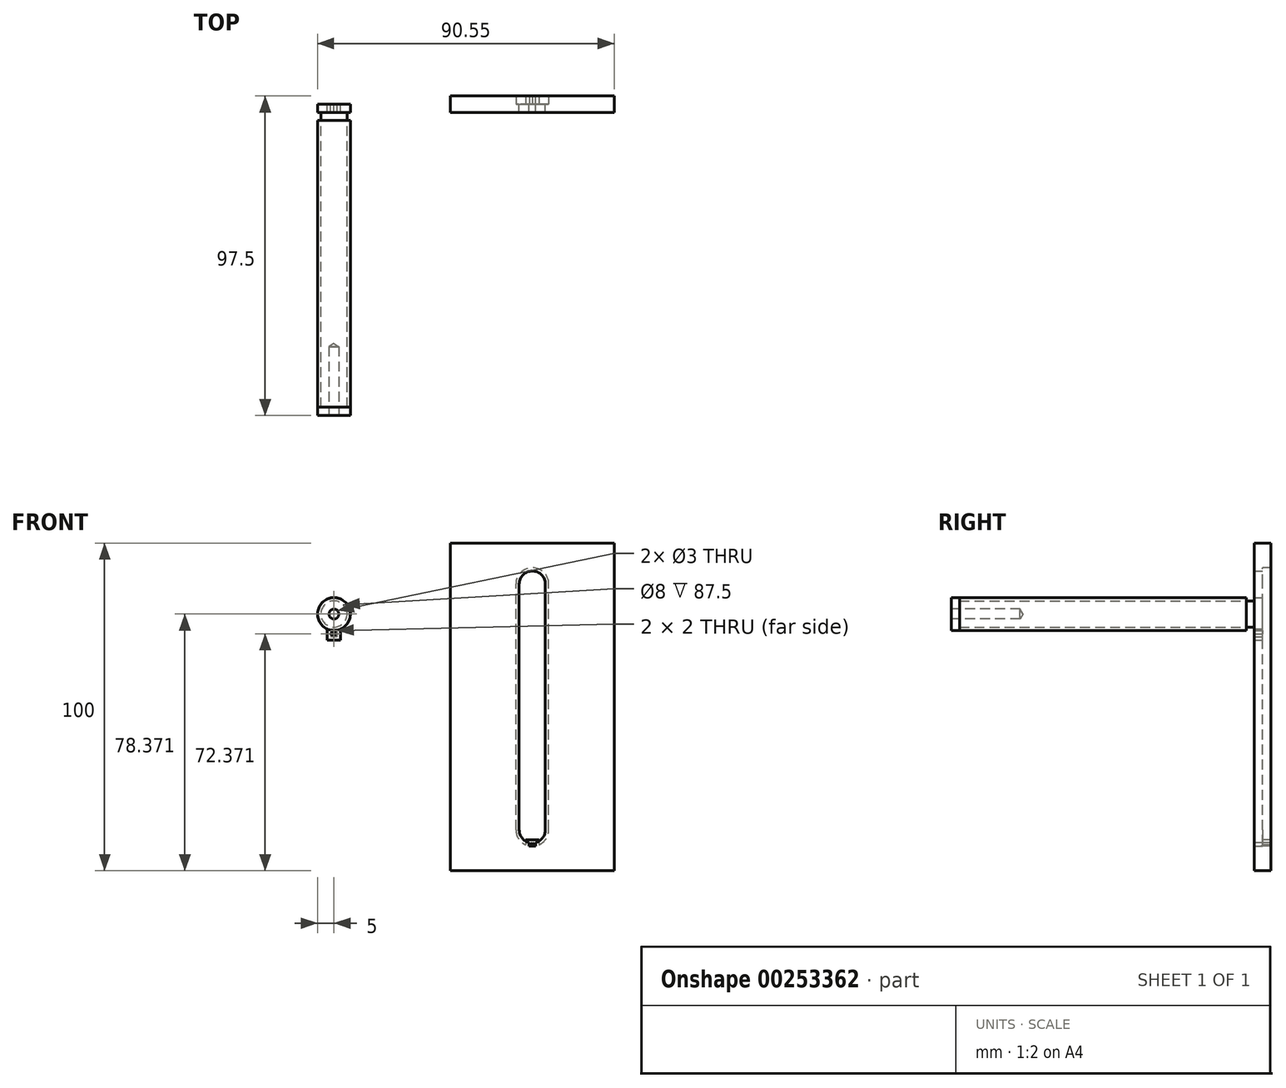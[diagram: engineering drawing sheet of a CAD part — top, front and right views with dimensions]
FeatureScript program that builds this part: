
annotation { "Feature Type Name" : "Feature", "Feature Type Description" : "" }
export const myFeature = defineFeature(function(context is Context, id is Id, definition is map)
    precondition{}
    {
        {
            var Q0;
            Q0=qCreatedBy(makeId("Front.planeOp"),FACE);
            var sketch = newSketch(context, id + "F0", { "sketchPlane" : qUnion([Q0])});
            skLineSegment(sketch, "E0.bottom", {"start": v(25, -50) * mm, "end": v(-25, -50) * mm});
            skLineSegment(sketch, "E0.top", {"start": v(25, 50) * mm, "end": v(-25, 50) * mm});
            skLineSegment(sketch, "E0.left", {"start": v(25, -50) * mm, "end": v(25, 50) * mm});
            skLineSegment(sketch, "E0.right", {"start": v(-25, -50) * mm, "end": v(-25, 50) * mm});
            skPoint(sketch, "E0.middle", {"position": v(0, 0) * mm});
            skArc(sketch, "E1", {"start": v(5, 37.5) * mm, "mid": v(0, 42.5) * mm, "end": v(-5, 37.5) * mm});
            skArc(sketch, "E2", {"start": v(-5, -37.5) * mm, "mid": v(0, -42.5) * mm, "end": v(5, -37.5) * mm});
            skLineSegment(sketch, "E3.left", {"start": v(5, -37.5) * mm, "end": v(5, 37.5) * mm});
            skLineSegment(sketch, "E3.right", {"start": v(-5, -37.5) * mm, "end": v(-5, 37.5) * mm});
            skPoint(sketch, "E4.end.orphan", {"position": v(0, 50) * mm});
            skArc(sketch, "E5", {"start": v(4, 37.5) * mm, "mid": v(0, 41.5) * mm, "end": v(-4, 37.5) * mm});
            skArc(sketch, "E6", {"start": v(-4, -37.5) * mm, "mid": v(0, -41.5) * mm, "end": v(4, -37.5) * mm});
            skLineSegment(sketch, "E7.left", {"start": v(-4, -37.5) * mm, "end": v(-4, 37.5) * mm});
            skLineSegment(sketch, "E7.right", {"start": v(4, -37.5) * mm, "end": v(4, 37.5) * mm});
            skLineSegment(sketch, "E8", {"start": v(0, -41.5) * mm, "end": v(0, -42.5) * mm});
            skLineSegment(sketch, "E9", {"start": v(0, -42.5) * mm, "end": v(-1, -42.5) * mm});
            skLineSegment(sketch, "E10", {"start": v(-1, -42.5) * mm, "end": v(0, -41.5) * mm});
            skLineSegment(sketch, "E11", {"start": v(0, -42.5) * mm, "end": v(1, -42.5) * mm});
            skLineSegment(sketch, "E12", {"start": v(1, -42.5) * mm, "end": v(0, -41.5) * mm});
            skLineSegment(sketch, "E13", {"start": v(0, -41.5) * mm, "end": v(0, -40.5) * mm});
            skLineSegment(sketch, "E14", {"start": v(0, -40.5) * mm, "end": v(1, -40.5) * mm});
            skLineSegment(sketch, "E15", {"start": v(1, -40.5) * mm, "end": v(1, -42.5) * mm});
            skLineSegment(sketch, "E16", {"start": v(0, -40.5) * mm, "end": v(-1, -40.5) * mm});
            skLineSegment(sketch, "E17", {"start": v(-1, -40.5) * mm, "end": v(-1, -42.5) * mm});
            skLineSegment(sketch, "E18", {"start": v(-1, -40.5) * mm, "end": v(-2, -40.5) * mm});
            skLineSegment(sketch, "E19", {"start": v(-2, -40.5) * mm, "end": v(-2, -42.5) * mm});
            skLineSegment(sketch, "E20", {"start": v(-2, -42.5) * mm, "end": v(-1, -42.5) * mm});
            skLineSegment(sketch, "E21", {"start": v(1, -40.5) * mm, "end": v(2, -40.5) * mm});
            skLineSegment(sketch, "E22", {"start": v(2, -40.5) * mm, "end": v(2, -42.5) * mm});
            skLineSegment(sketch, "E23", {"start": v(2, -42.5) * mm, "end": v(1, -42.5) * mm});
            skSolve(sketch);
        }
        {
            var Q0;
            Q0 = qSketchRegion(id + "F0", true);
            var Q1;
            {var subQ0=sQuery(id+"F0.wireOp",EDGE,"E9");Q1=makeQuery(id+"F0.imprint","IMPRINT",FACE,{"disambiguationData":[TD([[makeQuery(id+"F0.imprint","IMPRINT",EDGE,{"derivedFrom":subQ0}),-1.0]])]});}
            var Q2;
            {var subQ0=sQuery(id+"F0.wireOp",EDGE,"E17");var subQ1=sQuery(id+"F0.wireOp",EDGE,"E2");var subQ2=makeQuery(id+"F0.imprint","INTERSECT",VERTEX,{"derivedFrom":[subQ1,subQ0]});Q2=makeQuery(id+"F0.imprint","IMPRINT",FACE,{"disambiguationData":[TD([[makeQuery(id+"F0.imprint","IMPRINT",EDGE,{"disambiguationData":[TD([[subQ2,-1.0]])],"derivedFrom":subQ1}),-1.0]])]});}
            var Q3;
            {var subQ0=sQuery(id+"F0.wireOp",EDGE,"E12");var subQ1=sQuery(id+"F0.wireOp",EDGE,"E2");var subQ2=makeQuery(id+"F0.imprint","INTERSECT",VERTEX,{"derivedFrom":[subQ1,subQ0]});Q3=makeQuery(id+"F0.imprint","IMPRINT",FACE,{"disambiguationData":[TD([[makeQuery(id+"F0.imprint","IMPRINT",EDGE,{"disambiguationData":[TD([[subQ2,-1.0]])],"derivedFrom":subQ1}),-1.0]])]});}
            var Q4;
            {var subQ0=sQuery(id+"F0.wireOp",EDGE,"E11");Q4=makeQuery(id+"F0.imprint","IMPRINT",FACE,{"disambiguationData":[TD([[makeQuery(id+"F0.imprint","IMPRINT",EDGE,{"derivedFrom":subQ0}),1.0]])]});}
            var Q5;
            {var subQ0=sQuery(id+"F0.wireOp",EDGE,"E12");var subQ1=sQuery(id+"F0.wireOp",EDGE,"E2");var subQ2=makeQuery(id+"F0.imprint","INTERSECT",VERTEX,{"derivedFrom":[subQ1,subQ0]});Q5=makeQuery(id+"F0.imprint","IMPRINT",FACE,{"disambiguationData":[TD([[makeQuery(id+"F0.imprint","IMPRINT",EDGE,{"disambiguationData":[TD([[subQ2,-1.0]])],"derivedFrom":subQ1}),1.0]])]});}
            var Q6;
            {var subQ0=sQuery(id+"F0.wireOp",EDGE,"E13");Q6=makeQuery(id+"F0.imprint","IMPRINT",FACE,{"disambiguationData":[TD([[makeQuery(id+"F0.imprint","IMPRINT",EDGE,{"derivedFrom":subQ0}),-1.0]])]});}
            var Q7;
            {var subQ0=sQuery(id+"F0.wireOp",EDGE,"E13");Q7=makeQuery(id+"F0.imprint","IMPRINT",FACE,{"disambiguationData":[TD([[makeQuery(id+"F0.imprint","IMPRINT",EDGE,{"derivedFrom":subQ0}),1.0]])]});}
            var Q8;
            {var subQ0=sQuery(id+"F0.wireOp",EDGE,"E17");var subQ1=sQuery(id+"F0.wireOp",EDGE,"E2");var subQ2=makeQuery(id+"F0.imprint","INTERSECT",VERTEX,{"derivedFrom":[subQ1,subQ0]});Q8=makeQuery(id+"F0.imprint","IMPRINT",FACE,{"disambiguationData":[TD([[makeQuery(id+"F0.imprint","IMPRINT",EDGE,{"disambiguationData":[TD([[subQ2,-1.0]])],"derivedFrom":subQ1}),1.0]])]});}
            var Q9;
            {var subQ5=sQuery(id+"F0.wireOp",EDGE,"E18");Q9=makeQuery(id+"F0.imprint","IMPRINT",FACE,{"disambiguationData":[TD([[makeQuery(id+"F0.imprint","IMPRINT",EDGE,{"derivedFrom":subQ5}),1.0]])]});}
            var Q10;
            {var subQ0=sQuery(id+"F0.wireOp",EDGE,"E19");var subQ1=sQuery(id+"F0.wireOp",EDGE,"E2");var subQ2=makeQuery(id+"F0.imprint","INTERSECT",VERTEX,{"derivedFrom":[subQ1,subQ0]});Q10=makeQuery(id+"F0.imprint","IMPRINT",FACE,{"disambiguationData":[TD([[makeQuery(id+"F0.imprint","IMPRINT",EDGE,{"disambiguationData":[TD([[subQ2,-1.0]])],"derivedFrom":subQ1}),1.0]])]});}
            var Q11;
            {var subQ5=sQuery(id+"F0.wireOp",EDGE,"E20");Q11=makeQuery(id+"F0.imprint","IMPRINT",FACE,{"disambiguationData":[TD([[makeQuery(id+"F0.imprint","IMPRINT",EDGE,{"derivedFrom":subQ5}),1.0]])]});}
            var Q12;
            {var subQ5=sQuery(id+"F0.wireOp",EDGE,"E21");Q12=makeQuery(id+"F0.imprint","IMPRINT",FACE,{"disambiguationData":[TD([[makeQuery(id+"F0.imprint","IMPRINT",EDGE,{"derivedFrom":subQ5}),-1.0]])]});}
            var Q13;
            {var subQ0=sQuery(id+"F0.wireOp",EDGE,"E15");var subQ1=sQuery(id+"F0.wireOp",EDGE,"E2");var subQ2=makeQuery(id+"F0.imprint","INTERSECT",VERTEX,{"derivedFrom":[subQ1,subQ0]});Q13=makeQuery(id+"F0.imprint","IMPRINT",FACE,{"disambiguationData":[TD([[makeQuery(id+"F0.imprint","IMPRINT",EDGE,{"disambiguationData":[TD([[subQ2,-1.0]])],"derivedFrom":subQ1}),1.0]])]});}
            var Q14;
            {var subQ5=sQuery(id+"F0.wireOp",EDGE,"E23");Q14=makeQuery(id+"F0.imprint","IMPRINT",FACE,{"disambiguationData":[TD([[makeQuery(id+"F0.imprint","IMPRINT",EDGE,{"derivedFrom":subQ5}),-1.0]])]});}
            extrude(context, id + "F1", {"entities" : qUnion([Q0, Q1, Q2, Q3, Q4, Q5, Q6, Q7, Q8, Q9, Q10, Q11, Q12, Q13, Q14]), "oppositeDirection" : true, "depth" : 2.5 * mm});
        }
        {
            var Q0;
            Q0=makeQuery(id+"F0.imprint","IMPRINT",FACE,{"disambiguationData":[TD([[makeQuery(id+"F0.imprint","IMPRINT",EDGE,{"derivedFrom":sQuery(id+"F0.wireOp",EDGE,"E0.bottom")}),-1.0]])]});
            var Q1;
            Q1=makeQuery(id+"F0.imprint","IMPRINT",FACE,{"disambiguationData":[TD([[makeQuery(id+"F0.imprint","IMPRINT",EDGE,{"derivedFrom":sQuery(id+"F0.wireOp",EDGE,"E1")}),1.0]])]});
            var Q2;
            {var subQ0=sQuery(id+"F0.wireOp",EDGE,"E19");var subQ1=sQuery(id+"F0.wireOp",EDGE,"E2");var subQ2=makeQuery(id+"F0.imprint","INTERSECT",VERTEX,{"derivedFrom":[subQ1,subQ0]});Q2=makeQuery(id+"F0.imprint","IMPRINT",FACE,{"disambiguationData":[TD([[makeQuery(id+"F0.imprint","IMPRINT",EDGE,{"disambiguationData":[TD([[subQ2,-1.0]])],"derivedFrom":subQ1}),1.0]])]});}
            var Q3;
            {var subQ0=sQuery(id+"F0.wireOp",EDGE,"E15");var subQ1=sQuery(id+"F0.wireOp",EDGE,"E2");var subQ2=makeQuery(id+"F0.imprint","INTERSECT",VERTEX,{"derivedFrom":[subQ1,subQ0]});Q3=makeQuery(id+"F0.imprint","IMPRINT",FACE,{"disambiguationData":[TD([[makeQuery(id+"F0.imprint","IMPRINT",EDGE,{"disambiguationData":[TD([[subQ2,-1.0]])],"derivedFrom":subQ1}),1.0]])]});}
            var Q4;
            {var subQ5=sQuery(id+"F0.wireOp",EDGE,"E23");Q4=makeQuery(id+"F0.imprint","IMPRINT",FACE,{"disambiguationData":[TD([[makeQuery(id+"F0.imprint","IMPRINT",EDGE,{"derivedFrom":subQ5}),-1.0]])]});}
            var Q5;
            {var subQ5=sQuery(id+"F0.wireOp",EDGE,"E20");Q5=makeQuery(id+"F0.imprint","IMPRINT",FACE,{"disambiguationData":[TD([[makeQuery(id+"F0.imprint","IMPRINT",EDGE,{"derivedFrom":subQ5}),1.0]])]});}
            var Q6;
            {var subQ0=sQuery(id+"F0.wireOp",EDGE,"E17");var subQ1=sQuery(id+"F0.wireOp",EDGE,"E2");var subQ2=makeQuery(id+"F0.imprint","INTERSECT",VERTEX,{"derivedFrom":[subQ1,subQ0]});Q6=makeQuery(id+"F0.imprint","IMPRINT",FACE,{"disambiguationData":[TD([[makeQuery(id+"F0.imprint","IMPRINT",EDGE,{"disambiguationData":[TD([[subQ2,-1.0]])],"derivedFrom":subQ1}),-1.0]])]});}
            var Q7;
            {var subQ0=sQuery(id+"F0.wireOp",EDGE,"E9");Q7=makeQuery(id+"F0.imprint","IMPRINT",FACE,{"disambiguationData":[TD([[makeQuery(id+"F0.imprint","IMPRINT",EDGE,{"derivedFrom":subQ0}),-1.0]])]});}
            var Q8;
            {var subQ0=sQuery(id+"F0.wireOp",EDGE,"E12");var subQ1=sQuery(id+"F0.wireOp",EDGE,"E2");var subQ2=makeQuery(id+"F0.imprint","INTERSECT",VERTEX,{"derivedFrom":[subQ1,subQ0]});Q8=makeQuery(id+"F0.imprint","IMPRINT",FACE,{"disambiguationData":[TD([[makeQuery(id+"F0.imprint","IMPRINT",EDGE,{"disambiguationData":[TD([[subQ2,-1.0]])],"derivedFrom":subQ1}),-1.0]])]});}
            var Q9;
            {var subQ0=sQuery(id+"F0.wireOp",EDGE,"E11");Q9=makeQuery(id+"F0.imprint","IMPRINT",FACE,{"disambiguationData":[TD([[makeQuery(id+"F0.imprint","IMPRINT",EDGE,{"derivedFrom":subQ0}),1.0]])]});}
            extrude(context, id + "F2", {"entities" : qUnion([Q0, Q1, Q2, Q3, Q4, Q5, Q6, Q7, Q8, Q9]), "operationType" : NewBodyOperationType.ADD, "depth" : 2.5 * mm});
        }
        {
            var Q0;
            Q0=qCreatedBy(makeId("Front.planeOp"),FACE);
            var sketch = newSketch(context, id + "F3", { "sketchPlane" : qUnion([Q0])});
            skCircle(sketch, "E24", {"center": v(-60.55, 28.37) * mm, "radius": 5 * mm});
            skCircle(sketch, "E25", {"center": v(-60.55, 28.37) * mm, "radius": 4 * mm});
            skLineSegment(sketch, "E26", {"start": v(-59.55, 22.37) * mm, "end": v(-59.55, 21.37) * mm});
            skLineSegment(sketch, "E27", {"start": v(-59.55, 21.37) * mm, "end": v(-61.55, 21.37) * mm});
            skLineSegment(sketch, "E28", {"start": v(-61.55, 21.37) * mm, "end": v(-61.55, 22.37) * mm});
            skLineSegment(sketch, "E29", {"start": v(-59.55, 22.37) * mm, "end": v(-59.55, 23.47) * mm});
            skPoint(sketch, "E30.end.orphan", {"position": v(-60.55, 22.37) * mm});
            skPoint(sketch, "E30.start.orphan", {"position": v(-60.55, 23.37) * mm});
            skLineSegment(sketch, "E31", {"start": v(-60.55, 23.37) * mm, "end": v(-59.55, 22.37) * mm});
            skLineSegment(sketch, "E32", {"start": v(-61.55, 22.37) * mm, "end": v(-61.55, 23.47) * mm});
            skLineSegment(sketch, "E33", {"start": v(-60.55, 23.37) * mm, "end": v(-61.55, 22.37) * mm});
            skLineSegment(sketch, "E34", {"start": v(-61.55, 21.37) * mm, "end": v(-62.55, 21.37) * mm});
            skLineSegment(sketch, "E35", {"start": v(-62.55, 21.37) * mm, "end": v(-62.55, 23.79) * mm});
            skLineSegment(sketch, "E36", {"start": v(-59.55, 21.37) * mm, "end": v(-58.55, 21.37) * mm});
            skLineSegment(sketch, "E37", {"start": v(-58.55, 21.37) * mm, "end": v(-58.55, 23.79) * mm});
            skLineSegment(sketch, "E38", {"start": v(-62.55, 21.37) * mm, "end": v(-62.55, 20.37) * mm});
            skLineSegment(sketch, "E39", {"start": v(-62.55, 20.37) * mm, "end": v(-58.55, 20.37) * mm});
            skLineSegment(sketch, "E40", {"start": v(-58.55, 20.37) * mm, "end": v(-58.55, 21.37) * mm});
            skLineSegment(sketch, "E41", {"start": v(-61.55, 22.37) * mm, "end": v(-60.55, 21.37) * mm});
            skLineSegment(sketch, "E42", {"start": v(-60.55, 21.37) * mm, "end": v(-59.55, 22.37) * mm});
            skSolve(sketch);
        }
        {
            var Q0;
            Q0 = qSketchRegion(id + "F3", true);
            var Q1;
            {var subQ0=sQuery(id+"F3.wireOp",EDGE,"E28");Q1=makeQuery(id+"F3.imprint","IMPRINT",FACE,{"disambiguationData":[TD([[makeQuery(id+"F3.imprint","IMPRINT",EDGE,{"derivedFrom":subQ0}),-1.0]])]});}
            var Q2;
            {var subQ2=sQuery(id+"F3.wireOp",EDGE,"E32");Q2=makeQuery(id+"F3.imprint","IMPRINT",FACE,{"disambiguationData":[TD([[makeQuery(id+"F3.imprint","IMPRINT",EDGE,{"derivedFrom":subQ2}),-1.0]])]});}
            var Q3;
            {var subQ0=sQuery(id+"F3.wireOp",EDGE,"E29");Q3=makeQuery(id+"F3.imprint","IMPRINT",FACE,{"disambiguationData":[TD([[makeQuery(id+"F3.imprint","IMPRINT",EDGE,{"derivedFrom":subQ0}),1.0]])]});}
            var Q4;
            {var subQ0=sQuery(id+"F3.wireOp",EDGE,"E26");Q4=makeQuery(id+"F3.imprint","IMPRINT",FACE,{"disambiguationData":[TD([[makeQuery(id+"F3.imprint","IMPRINT",EDGE,{"derivedFrom":subQ0}),-1.0]])]});}
            extrude(context, id + "F4", {"entities" : qUnion([Q0, Q1, Q2, Q3, Q4]), "depth" : 2.5 * mm});
        }
        {
            var Q0;
            Q0=makeQuery(id+"F3.imprint","IMPRINT",FACE,{"disambiguationData":[TD([[makeQuery(id+"F3.imprint","IMPRINT",EDGE,{"derivedFrom":sQuery(id+"F3.wireOp",EDGE,"E25")}),1.0]])]});
            extrude(context, id + "F5", {"entities" : qUnion([Q0]), "operationType" : NewBodyOperationType.ADD, "depth" : 92.5 * mm});
        }
        {
            var Q0;
            Q0=makeQuery(id+"F5.opExtrude","CAP_FACE",FACE,{"disambiguationData":[OSD([sQuery(id+"F3.wireOp",EDGE,"E25")])],"isStart":false});
            var sketch = newSketch(context, id + "F6", { "sketchPlane" : qUnion([Q0])});
            skCircle(sketch, "E43", {"center": v(-60.55, 28.37) * mm, "radius": 4 * mm});
            skSolve(sketch);
        }
        {
            var Q0;
            Q0=makeQuery(id+"F3.imprint","IMPRINT",FACE,{"disambiguationData":[TD([[makeQuery(id+"F3.imprint","IMPRINT",EDGE,{"derivedFrom":sQuery(id+"F3.wireOp",EDGE,"E25")}),-1.0]])]});
            extrude(context, id + "F7", {"entities" : qUnion([Q0]), "depth" : 92.5 * mm, "hasSecondDirection" : true, "secondDirectionOppositeDirection" : false, "secondDirectionDepth" : 5 * mm});
        }
        {
            var Q0;
            Q0=sQuery(id+"F6.wireOp",VERTEX,"E43.center");
            var Q1;
            Q1=makeQuery(id+"F4.opExtrude","SWEPT_BODY",BODY,{"disambiguationData":[OSD([sQuery(id+"F3.wireOp",EDGE,"E24"),sQuery(id+"F3.wireOp",EDGE,"E25"),sQuery(id+"F3.wireOp",EDGE,"E31"),sQuery(id+"F3.wireOp",EDGE,"E33"),sQuery(id+"F3.wireOp",EDGE,"E35"),sQuery(id+"F3.wireOp",EDGE,"E37"),sQuery(id+"F3.wireOp",EDGE,"E38"),sQuery(id+"F3.wireOp",EDGE,"E39"),sQuery(id+"F3.wireOp",EDGE,"E40"),sQuery(id+"F3.wireOp",EDGE,"E41"),sQuery(id+"F3.wireOp",EDGE,"E42")])]});
            hole(context, id + "F8", {"style" : HoleStyle.SIMPLE, "endStyle" : HoleEndStyle.BLIND, "holeDiameter" : 3 * mm, "holeDepth" : 18.5 * mm, "tappedDepth" : 12 * mm, "tapClearance" : 3, "startFromSketch" : true, "locations" : qUnion([Q0]), "scope" : qUnion([Q1])});
        }
        {
            var Q0;
            Q0=makeQuery(id+"F3.imprint","IMPRINT",FACE,{"disambiguationData":[TD([[makeQuery(id+"F3.imprint","IMPRINT",EDGE,{"derivedFrom":sQuery(id+"F3.wireOp",EDGE,"E25")}),1.0]])]});
            var Q1;
            Q1=makeQuery(id+"F3.imprint","IMPRINT",FACE,{"disambiguationData":[TD([[makeQuery(id+"F3.imprint","IMPRINT",EDGE,{"derivedFrom":sQuery(id+"F3.wireOp",EDGE,"E25")}),-1.0]])]});
            extrude(context, id + "F9", {"entities" : qUnion([Q0, Q1]), "depth" : 95 * mm, "hasSecondDirection" : true, "secondDirectionOppositeDirection" : false, "secondDirectionDepth" : 92.5 * mm});
        }
        {
            var Q0;
            Q0=makeQuery(id+"F9.opExtrude","CAP_FACE",FACE,{"disambiguationData":[OSD([sQuery(id+"F3.wireOp",EDGE,"E24")])],"isStart":false});
            var sketch = newSketch(context, id + "F10", { "sketchPlane" : qUnion([Q0])});
            skCircle(sketch, "E44", {"center": v(-60.55, 28.37) * mm, "radius": 5 * mm});
            skSolve(sketch);
        }
        {
            var Q0;
            Q0=sQuery(id+"F10.wireOp",VERTEX,"E44.center");
            var Q1;
            Q1=makeQuery(id+"F9.opExtrude","SWEPT_BODY",BODY,{"disambiguationData":[OSD([sQuery(id+"F3.wireOp",EDGE,"E24")])]});
            hole(context, id + "F11", {"style" : HoleStyle.SIMPLE, "endStyle" : HoleEndStyle.BLIND, "holeDiameter" : 3 * mm, "holeDepth" : 18.5 * mm, "tappedDepth" : 12 * mm, "tapClearance" : 3, "startFromSketch" : true, "locations" : qUnion([Q0]), "scope" : qUnion([Q1])});
        }
    });
